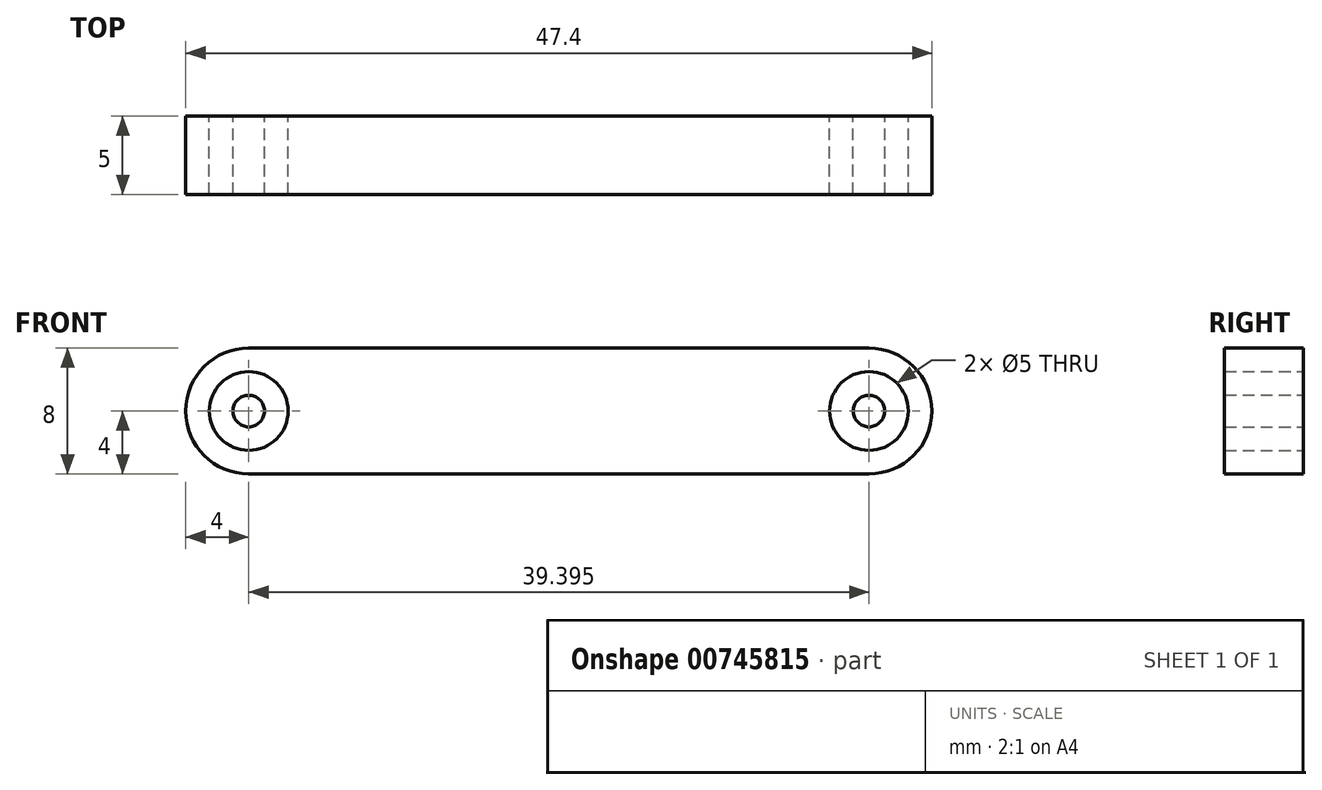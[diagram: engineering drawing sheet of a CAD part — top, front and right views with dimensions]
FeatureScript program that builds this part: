
annotation { "Feature Type Name" : "Feature", "Feature Type Description" : "" }
export const myFeature = defineFeature(function(context is Context, id is Id, definition is map)
    precondition{}
    {
        {
            var Q0;
            Q0=qCreatedBy(makeId("Front.planeOp"),FACE);
            var sketch = newSketch(context, id + "F0", { "sketchPlane" : qUnion([Q0])});
            skArc(sketch, "E0", {"start": v(0, 4) * mm, "mid": v(-4, 0) * mm, "end": v(0, -4) * mm});
            skCircle(sketch, "E1", {"center": v(0, 0) * mm, "radius": 2.5 * mm});
            skCircle(sketch, "E2", {"center": v(0, 0) * mm, "radius": 1 * mm});
            skArc(sketch, "E3", {"start": v(39.4, -4) * mm, "mid": v(43.4, 0) * mm, "end": v(39.4, 4) * mm});
            skCircle(sketch, "E4", {"center": v(39.4, 0) * mm, "radius": 2.5 * mm});
            skCircle(sketch, "E5", {"center": v(39.4, 0) * mm, "radius": 1 * mm});
            skLineSegment(sketch, "E6", {"start": v(0, 4) * mm, "end": v(39.4, 4) * mm});
            skLineSegment(sketch, "E7", {"start": v(0, -4) * mm, "end": v(39.4, -4) * mm});
            skSolve(sketch);
        }
        {
            var Q0;
            Q0 = qSketchRegion(id + "F0", true);
            var Q1;
            Q1=makeQuery(id+"F0.imprint","IMPRINT",FACE,{"disambiguationData":[TD([[makeQuery(id+"F0.imprint","IMPRINT",EDGE,{"derivedFrom":sQuery(id+"F0.wireOp",EDGE,"E2")}),1.0]])]});
            var Q2;
            Q2=makeQuery(id+"F0.imprint","IMPRINT",FACE,{"disambiguationData":[TD([[makeQuery(id+"F0.imprint","IMPRINT",EDGE,{"derivedFrom":sQuery(id+"F0.wireOp",EDGE,"E5")}),1.0]])]});
            extrude(context, id + "F1", {"entities" : qUnion([Q0, Q1, Q2]), "depth" : 5 * mm, "offsetDistance" : 25.4 * mm});
        }
    });
